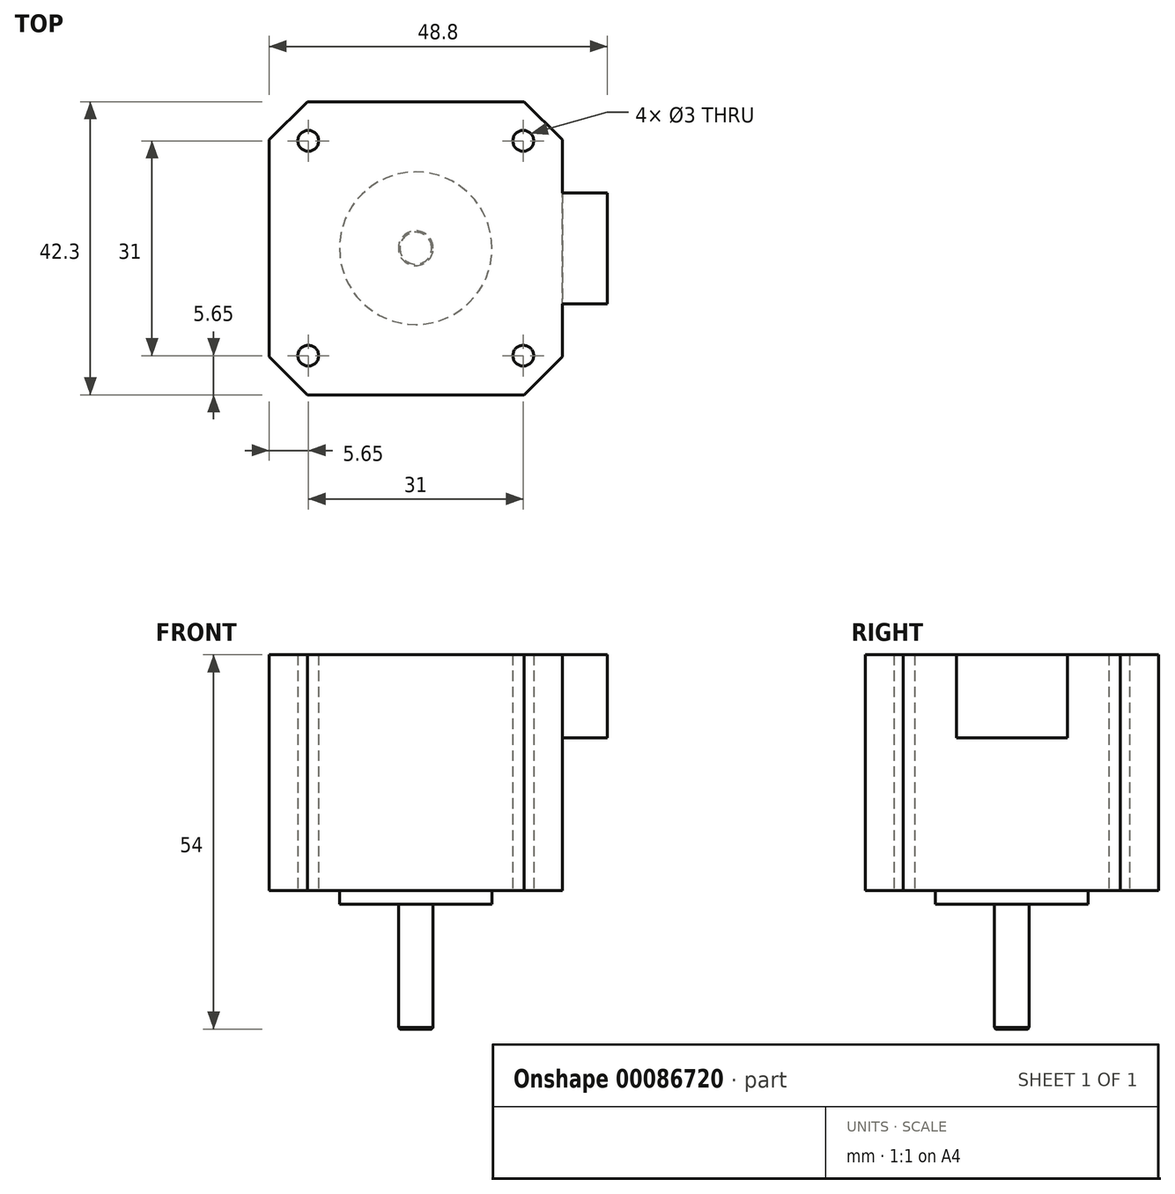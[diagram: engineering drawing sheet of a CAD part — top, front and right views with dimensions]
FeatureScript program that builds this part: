
annotation { "Feature Type Name" : "Feature", "Feature Type Description" : "" }
export const myFeature = defineFeature(function(context is Context, id is Id, definition is map)
    precondition{}
    {
        {
            var Q0;
            Q0=qCreatedBy(makeId("Top.planeOp"),FACE);
            var sketch = newSketch(context, id + "F0", { "sketchPlane" : qUnion([Q0])});
            skCircle(sketch, "E0", {"center": v(0, 0) * mm, "radius": 11 * mm});
            skLineSegment(sketch, "E1.bottom", {"start": v(21.15, -21.15) * mm, "end": v(-21.15, -21.15) * mm});
            skLineSegment(sketch, "E1.top", {"start": v(21.15, 21.15) * mm, "end": v(-21.15, 21.15) * mm});
            skLineSegment(sketch, "E1.left", {"start": v(21.15, -21.15) * mm, "end": v(21.15, 21.15) * mm});
            skLineSegment(sketch, "E1.right", {"start": v(-21.15, -21.15) * mm, "end": v(-21.15, 21.15) * mm});
            skCircle(sketch, "E2", {"center": v(0, 0) * mm, "radius": 2.5 * mm});
            skCircle(sketch, "E3", {"center": v(-15.5, 15.5) * mm, "radius": 1.5 * mm});
            skCircle(sketch, "E4", {"center": v(15.5, 15.5) * mm, "radius": 1.5 * mm});
            skCircle(sketch, "E5", {"center": v(15.5, -15.5) * mm, "radius": 1.5 * mm});
            skCircle(sketch, "E6", {"center": v(-15.5, -15.5) * mm, "radius": 1.5 * mm});
            skSolve(sketch);
        }
        {
            var Q0;
            Q0=makeQuery(id+"F0.imprint","IMPRINT",FACE,{"disambiguationData":[TD([[makeQuery(id+"F0.imprint","IMPRINT",EDGE,{"derivedFrom":sQuery(id+"F0.wireOp",EDGE,"E0")}),-1.0]])]});
            var Q1;
            Q1=makeQuery(id+"F0.imprint","IMPRINT",FACE,{"disambiguationData":[TD([[makeQuery(id+"F0.imprint","IMPRINT",EDGE,{"derivedFrom":sQuery(id+"F0.wireOp",EDGE,"E0")}),1.0]])]});
            var Q2;
            Q2=makeQuery(id+"F0.imprint","IMPRINT",FACE,{"disambiguationData":[TD([[makeQuery(id+"F0.imprint","IMPRINT",EDGE,{"derivedFrom":sQuery(id+"F0.wireOp",EDGE,"E2")}),1.0]])]});
            extrude(context, id + "F1", {"entities" : qUnion([Q0, Q1, Q2]), "depth" : 34 * mm});
        }
        {
            var Q0;
            Q0=makeQuery(id+"F0.imprint","IMPRINT",FACE,{"disambiguationData":[TD([[makeQuery(id+"F0.imprint","IMPRINT",EDGE,{"derivedFrom":sQuery(id+"F0.wireOp",EDGE,"E0")}),1.0]])]});
            extrude(context, id + "F2", {"entities" : qUnion([Q0]), "operationType" : NewBodyOperationType.ADD, "oppositeDirection" : true, "depth" : 2 * mm});
        }
        {
            var Q0;
            Q0=makeQuery(id+"F0.imprint","IMPRINT",FACE,{"disambiguationData":[TD([[makeQuery(id+"F0.imprint","IMPRINT",EDGE,{"derivedFrom":sQuery(id+"F0.wireOp",EDGE,"E2")}),1.0]])]});
            var Q1;
            Q1=sQuery(id+"F0.wireOp",EDGE,"E2");
            extrude(context, id + "F3", {"entities" : qUnion([Q0]), "operationType" : NewBodyOperationType.ADD, "surfaceEntities" : qUnion([Q1]), "oppositeDirection" : true, "depth" : 20 * mm});
        }
        {
            var Q0;
            Q0=makeQuery(id+"F1.opExtrude","SWEPT_EDGE",EDGE,{"disambiguationData":[OSD([sQuery(id+"F0.wireOp",EDGE,"E1.bottom"),sQuery(id+"F0.wireOp",EDGE,"E1.right")])]});
            var Q1;
            Q1=makeQuery(id+"F1.opExtrude","SWEPT_EDGE",EDGE,{"disambiguationData":[OSD([sQuery(id+"F0.wireOp",EDGE,"E1.bottom"),sQuery(id+"F0.wireOp",EDGE,"E1.left")])]});
            var Q2;
            Q2=makeQuery(id+"F1.opExtrude","SWEPT_EDGE",EDGE,{"disambiguationData":[OSD([sQuery(id+"F0.wireOp",EDGE,"E1.top"),sQuery(id+"F0.wireOp",EDGE,"E1.left")])]});
            var Q3;
            Q3=makeQuery(id+"F1.opExtrude","SWEPT_EDGE",EDGE,{"disambiguationData":[OSD([sQuery(id+"F0.wireOp",EDGE,"E1.top"),sQuery(id+"F0.wireOp",EDGE,"E1.right")])]});
            chamfer(context, id + "F4", {"entities" : qUnion([Q0, Q1, Q2, Q3]), "width" : 5.5 * mm, "tangentPropagation" : true});
        }
        {
            var Q0;
            Q0=makeQuery(id+"F3.opExtrude","CAP_EDGE",EDGE,{"disambiguationData":[OSD([sQuery(id+"F0.wireOp",EDGE,"E2")])],"isStart":false});
            chamfer(context, id + "F5", {"entities" : qUnion([Q0]), "width" : .2 * mm, "tangentPropagation" : true});
        }
        {
            var Q0;
            Q0=makeQuery(id+"F1.opExtrude","SWEPT_FACE",FACE,{"disambiguationData":[OSD([sQuery(id+"F0.wireOp",EDGE,"E1.left")])]});
            var sketch = newSketch(context, id + "F6", { "sketchPlane" : qUnion([Q0])});
            skLineSegment(sketch, "E7.bottom", {"start": v(8, 34) * mm, "end": v(-8, 34) * mm});
            skLineSegment(sketch, "E7.top", {"start": v(8, 22) * mm, "end": v(-8, 22) * mm});
            skLineSegment(sketch, "E7.left", {"start": v(8, 34) * mm, "end": v(8, 22) * mm});
            skLineSegment(sketch, "E7.right", {"start": v(-8, 34) * mm, "end": v(-8, 22) * mm});
            skPoint(sketch, "E7.middle", {"position": v(0, 28) * mm});
            skSolve(sketch);
        }
        {
            var Q0;
            Q0 = qSketchRegion(id + "F6", true);
            extrude(context, id + "F7", {"entities" : qUnion([Q0]), "operationType" : NewBodyOperationType.ADD, "depth" : 6.5 * mm});
        }
    });
